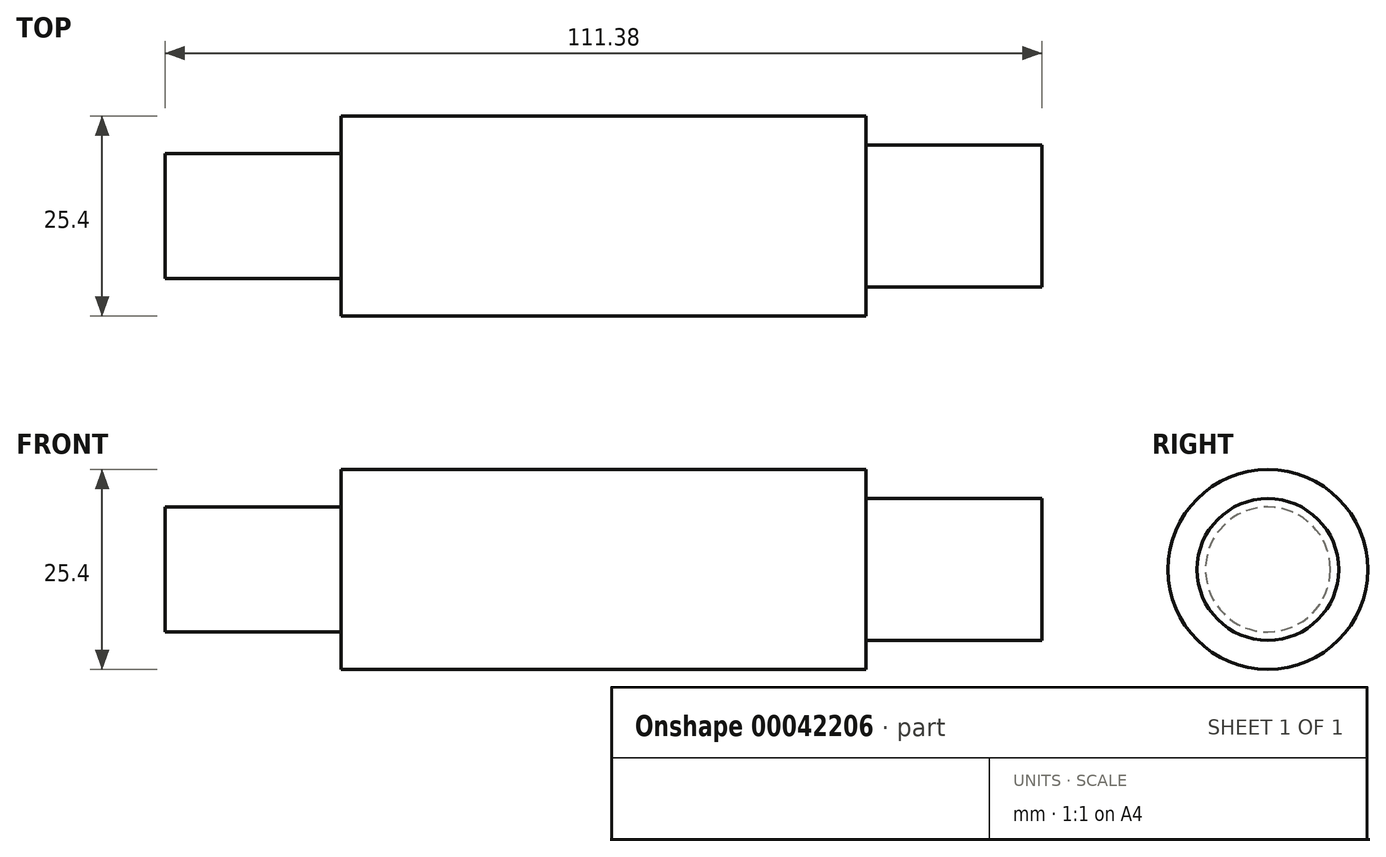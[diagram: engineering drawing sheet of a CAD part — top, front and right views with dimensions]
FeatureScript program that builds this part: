
annotation { "Feature Type Name" : "Feature", "Feature Type Description" : "" }
export const myFeature = defineFeature(function(context is Context, id is Id, definition is map)
    precondition{}
    {
        {
            var Q0;
            Q0=qCreatedBy(makeId("Right.planeOp"),FACE);
            var sketch = newSketch(context, id + "F0", { "sketchPlane" : qUnion([Q0])});
            skCircle(sketch, "E0", {"center": v(0, 0) * mm, "radius": 12.7 * mm});
            skSolve(sketch);
        }
        {
            var Q0;
            Q0 = qSketchRegion(id + "F0", true);
            extrude(context, id + "F1", {"entities" : qUnion([Q0]), "endBound" : BoundingType.SYMMETRIC, "depth" : 66.67 * mm});
        }
        {
            var Q0;
            Q0=makeQuery(id+"F1.opExtrude","CAP_FACE",FACE,{"disambiguationData":[OSD([sQuery(id+"F0.wireOp",EDGE,"E0")])],"isStart":false});
            var sketch = newSketch(context, id + "F2", { "sketchPlane" : qUnion([Q0])});
            skCircle(sketch, "E1", {"center": v(0, 0) * mm, "radius": 9 * mm});
            skSolve(sketch);
        }
        {
            var Q0;
            Q0 = qSketchRegion(id + "F2", true);
            extrude(context, id + "F3", {"entities" : qUnion([Q0]), "operationType" : NewBodyOperationType.ADD, "depth" : 22.35 * mm});
        }
        {
            var Q0;
            Q0=makeQuery(id+"F1.opExtrude","CAP_FACE",FACE,{"disambiguationData":[OSD([sQuery(id+"F0.wireOp",EDGE,"E0")])],"isStart":true});
            var sketch = newSketch(context, id + "F4", { "sketchPlane" : qUnion([Q0])});
            skCircle(sketch, "E2", {"center": v(0, 0) * mm, "radius": 7.94 * mm});
            skSolve(sketch);
        }
        {
            var Q0;
            Q0 = qSketchRegion(id + "F4", true);
            extrude(context, id + "F5", {"entities" : qUnion([Q0]), "operationType" : NewBodyOperationType.ADD, "depth" : 22.35 * mm});
        }
    });
